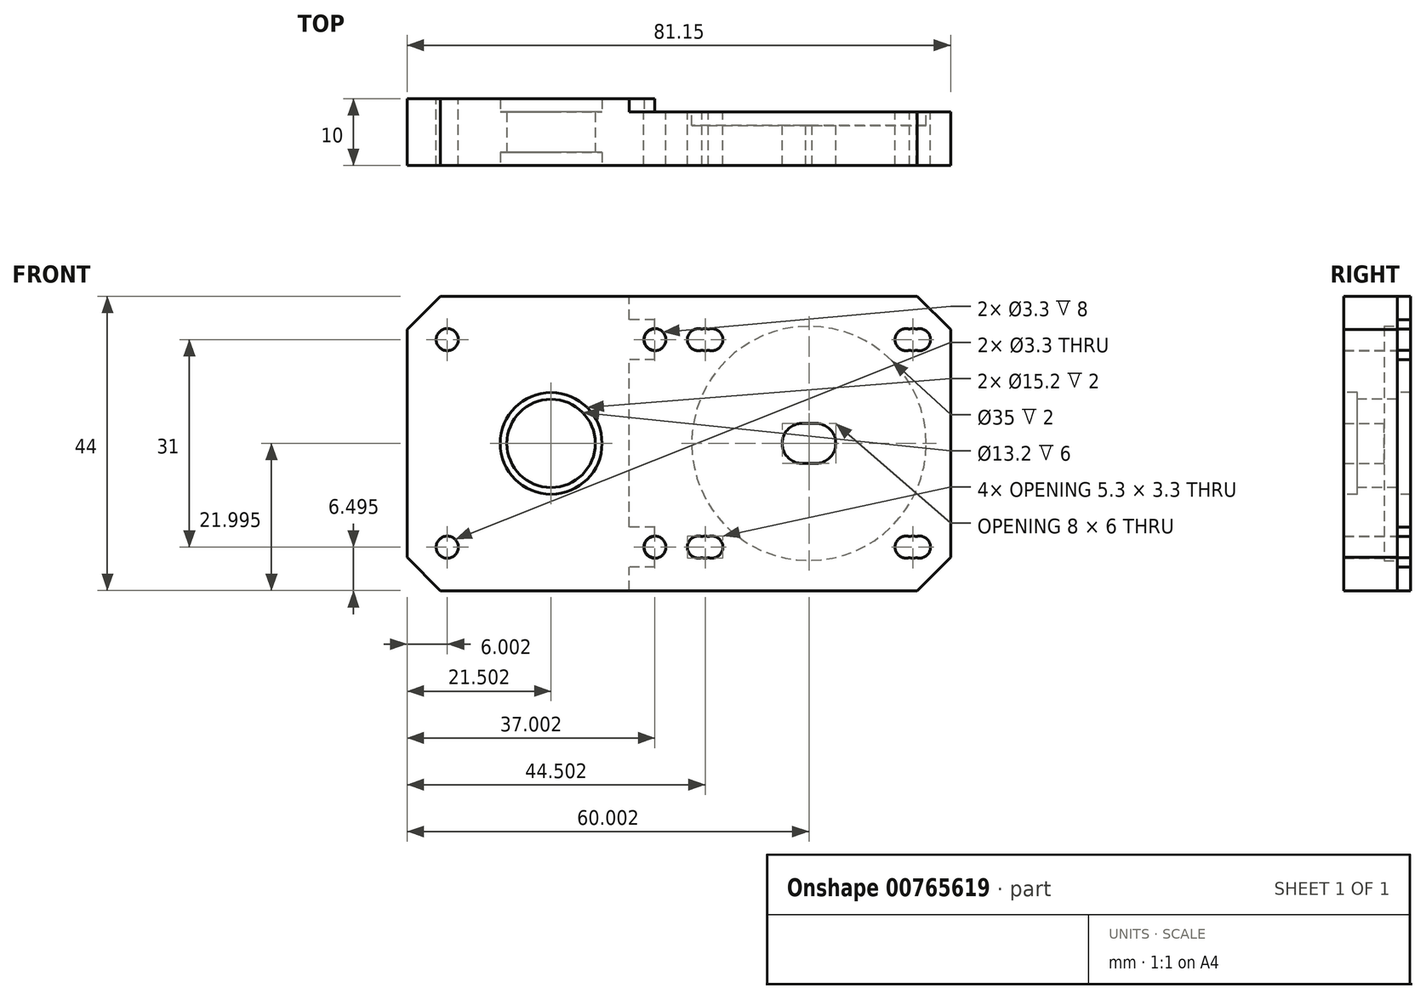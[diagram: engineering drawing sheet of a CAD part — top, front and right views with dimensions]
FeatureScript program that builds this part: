
annotation { "Feature Type Name" : "Feature", "Feature Type Description" : "" }
export const myFeature = defineFeature(function(context is Context, id is Id, definition is map)
    precondition{}
    {
        {
            var Q0;
            Q0=qCreatedBy(makeId("Front.planeOp"),FACE);
            var sketch = newSketch(context, id + "F0", { "sketchPlane" : qUnion([Q0])});
            skLineSegment(sketch, "E0.bottom", {"start": v(-213.07, -45.16) * mm, "end": v(-131.92, -45.16) * mm});
            skLineSegment(sketch, "E0.top", {"start": v(-213.07, -89.16) * mm, "end": v(-131.92, -89.16) * mm});
            skLineSegment(sketch, "E0.left", {"start": v(-213.07, -45.16) * mm, "end": v(-213.07, -89.16) * mm});
            skLineSegment(sketch, "E0.right", {"start": v(-131.92, -45.16) * mm, "end": v(-131.92, -89.16) * mm});
            skLineSegment(sketch, "E1", {"start": v(-131.92, -67.16) * mm, "end": v(-153.07, -67.16) * mm, "construction": true});
            skArc(sketch, "E2", {"start": v(-153.57, -70.12) * mm, "mid": v(-153.07, -70.16) * mm, "end": v(-152.57, -70.12) * mm});
            skLineSegment(sketch, "E3", {"start": v(-153.07, -67.16) * mm, "end": v(-191.57, -67.16) * mm, "construction": true});
            skCircle(sketch, "E4", {"center": v(-191.57, -67.16) * mm, "radius": 3 * mm});
            skLineSegment(sketch, "E5", {"start": v(-191.57, -67.16) * mm, "end": v(-213.07, -67.16) * mm, "construction": true});
            skLineSegment(sketch, "E6.bottom", {"start": v(-137.57, -82.66) * mm, "end": v(-168.57, -82.66) * mm, "construction": true});
            skLineSegment(sketch, "E6.top", {"start": v(-137.57, -51.66) * mm, "end": v(-168.57, -51.66) * mm, "construction": true});
            skLineSegment(sketch, "E6.left", {"start": v(-137.57, -82.66) * mm, "end": v(-137.57, -51.66) * mm, "construction": true});
            skLineSegment(sketch, "E6.right", {"start": v(-168.57, -82.66) * mm, "end": v(-168.57, -51.66) * mm, "construction": true});
            skArc(sketch, "E7", {"start": v(-169.07, -53.24) * mm, "mid": v(-168.57, -53.31) * mm, "end": v(-168.07, -53.24) * mm});
            skArc(sketch, "E8", {"start": v(-138.07, -53.24) * mm, "mid": v(-137.57, -53.31) * mm, "end": v(-137.07, -53.24) * mm});
            skArc(sketch, "E9", {"start": v(-169.07, -84.24) * mm, "mid": v(-168.57, -84.31) * mm, "end": v(-168.07, -84.24) * mm});
            skArc(sketch, "E10", {"start": v(-138.07, -84.24) * mm, "mid": v(-137.57, -84.31) * mm, "end": v(-137.07, -84.24) * mm});
            skLineSegment(sketch, "E11.bottom", {"start": v(-176.07, -51.66) * mm, "end": v(-207.07, -51.66) * mm, "construction": true});
            skLineSegment(sketch, "E11.top", {"start": v(-176.07, -82.66) * mm, "end": v(-207.07, -82.66) * mm, "construction": true});
            skLineSegment(sketch, "E11.left", {"start": v(-176.07, -51.66) * mm, "end": v(-176.07, -82.66) * mm, "construction": true});
            skLineSegment(sketch, "E11.right", {"start": v(-207.07, -51.66) * mm, "end": v(-207.07, -82.66) * mm, "construction": true});
            skCircle(sketch, "E12", {"center": v(-176.07, -51.66) * mm, "radius": 1.65 * mm});
            skCircle(sketch, "E13", {"center": v(-207.07, -51.66) * mm, "radius": 1.65 * mm});
            skCircle(sketch, "E14", {"center": v(-207.07, -82.66) * mm, "radius": 1.65 * mm});
            skCircle(sketch, "E15", {"center": v(-176.07, -82.66) * mm, "radius": 1.65 * mm});
            skLineSegment(sketch, "E16", {"start": v(-168.57, -51.66) * mm, "end": v(-169.57, -51.66) * mm, "construction": true});
            skLineSegment(sketch, "E17", {"start": v(-169.57, -51.66) * mm, "end": v(-168.57, -51.66) * mm, "construction": true});
            skLineSegment(sketch, "E18", {"start": v(-167.57, -51.66) * mm, "end": v(-168.57, -51.66) * mm, "construction": true});
            skArc(sketch, "E19", {"start": v(-168.07, -53.24) * mm, "mid": v(-165.92, -51.66) * mm, "end": v(-168.07, -50.1) * mm});
            skArc(sketch, "E20", {"start": v(-169.07, -50.1) * mm, "mid": v(-171.22, -51.66) * mm, "end": v(-169.07, -53.24) * mm});
            skArc(sketch, "E21.MirrorC", {"start": v(-168.07, -81.1) * mm, "mid": v(-165.92, -82.66) * mm, "end": v(-168.07, -84.24) * mm});
            skArc(sketch, "E22.MirrorC", {"start": v(-169.07, -84.24) * mm, "mid": v(-171.22, -82.66) * mm, "end": v(-169.07, -81.1) * mm});
            skLineSegment(sketch, "E23", {"start": v(-153.07, -51.66) * mm, "end": v(-153.07, -82.66) * mm, "construction": true});
            skArc(sketch, "E24.MirrorC", {"start": v(-138.07, -53.24) * mm, "mid": v(-140.22, -51.66) * mm, "end": v(-138.07, -50.1) * mm});
            skArc(sketch, "E25.MirrorC", {"start": v(-137.07, -50.1) * mm, "mid": v(-134.92, -51.66) * mm, "end": v(-137.07, -53.24) * mm});
            skArc(sketch, "E26.MirrorC", {"start": v(-137.07, -84.24) * mm, "mid": v(-134.92, -82.66) * mm, "end": v(-137.07, -81.1) * mm});
            skArc(sketch, "E27.MirrorC", {"start": v(-138.07, -81.1) * mm, "mid": v(-140.22, -82.66) * mm, "end": v(-138.07, -84.24) * mm});
            skArc(sketch, "E28.trimOffspring", {"start": v(-168.07, -50.1) * mm, "mid": v(-168.57, -50.01) * mm, "end": v(-169.07, -50.1) * mm});
            skArc(sketch, "E29.trimOffspring", {"start": v(-168.07, -81.1) * mm, "mid": v(-168.57, -81.01) * mm, "end": v(-169.07, -81.1) * mm});
            skArc(sketch, "E30.trimOffspring", {"start": v(-137.07, -81.1) * mm, "mid": v(-137.57, -81.01) * mm, "end": v(-138.07, -81.1) * mm});
            skArc(sketch, "E31.trimOffspring", {"start": v(-137.07, -50.1) * mm, "mid": v(-137.57, -50.01) * mm, "end": v(-138.07, -50.1) * mm});
            skLineSegment(sketch, "E32", {"start": v(-153.07, -67.16) * mm, "end": v(-154.07, -67.16) * mm, "construction": true});
            skLineSegment(sketch, "E33", {"start": v(-153.07, -67.16) * mm, "end": v(-152.07, -67.16) * mm, "construction": true});
            skArc(sketch, "E34", {"start": v(-152.57, -70.12) * mm, "mid": v(-149.07, -67.16) * mm, "end": v(-152.57, -64.2) * mm});
            skArc(sketch, "E35", {"start": v(-153.57, -64.2) * mm, "mid": v(-157.07, -67.16) * mm, "end": v(-153.57, -70.12) * mm});
            skArc(sketch, "E36.trimOffspring", {"start": v(-152.57, -64.2) * mm, "mid": v(-153.07, -64.16) * mm, "end": v(-153.57, -64.2) * mm});
            skSolve(sketch);
        }
        {
            var Q0;
            Q0 = qSketchRegion(id + "F0", true);
            extrude(context, id + "F1", {"entities" : qUnion([Q0]), "depth" : 8 * mm, "offsetDistance" : 25 * mm});
        }
        {
            var Q0;
            Q0=makeQuery(id+"F1.opExtrude","CAP_FACE",FACE,{"disambiguationData":[OSD([sQuery(id+"F0.wireOp",EDGE,"E0.bottom"),sQuery(id+"F0.wireOp",EDGE,"E0.top"),sQuery(id+"F0.wireOp",EDGE,"E0.left"),sQuery(id+"F0.wireOp",EDGE,"E0.right"),sQuery(id+"F0.wireOp",EDGE,"E2"),sQuery(id+"F0.wireOp",EDGE,"E4"),sQuery(id+"F0.wireOp",EDGE,"E7"),sQuery(id+"F0.wireOp",EDGE,"E8"),sQuery(id+"F0.wireOp",EDGE,"E9"),sQuery(id+"F0.wireOp",EDGE,"E10")])],"isStart":true});
            var sketch = newSketch(context, id + "F2", { "sketchPlane" : qUnion([Q0])});
            skCircle(sketch, "E37", {"center": v(153.07, -67.16) * mm, "radius": 17.5 * mm});
            skSolve(sketch);
        }
        {
            var Q0;
            Q0 = qSketchRegion(id + "F2", true);
            extrude(context, id + "F3", {"entities" : qUnion([Q0]), "operationType" : NewBodyOperationType.REMOVE, "oppositeDirection" : true, "depth" : 2 * mm, "offsetDistance" : 25 * mm});
        }
        {
            var Q0;
            Q0=makeQuery(id+"F1.opExtrude","CAP_FACE",FACE,{"disambiguationData":[OSD([sQuery(id+"F0.wireOp",EDGE,"E0.bottom"),sQuery(id+"F0.wireOp",EDGE,"E0.top"),sQuery(id+"F0.wireOp",EDGE,"E0.left"),sQuery(id+"F0.wireOp",EDGE,"E0.right"),sQuery(id+"F0.wireOp",EDGE,"E2"),sQuery(id+"F0.wireOp",EDGE,"E4"),sQuery(id+"F0.wireOp",EDGE,"E7"),sQuery(id+"F0.wireOp",EDGE,"E8"),sQuery(id+"F0.wireOp",EDGE,"E9"),sQuery(id+"F0.wireOp",EDGE,"E10")])],"isStart":true});
            var sketch = newSketch(context, id + "F4", { "sketchPlane" : qUnion([Q0])});
            skLineSegment(sketch, "E38.bottom", {"start": v(131.92, -89.16) * mm, "end": v(179.92, -89.16) * mm, "construction": true});
            skLineSegment(sketch, "E38.top", {"start": v(131.92, -45.16) * mm, "end": v(179.92, -45.16) * mm, "construction": true});
            skLineSegment(sketch, "E38.left", {"start": v(131.92, -89.16) * mm, "end": v(131.92, -45.16) * mm, "construction": true});
            skLineSegment(sketch, "E38.right", {"start": v(179.92, -89.16) * mm, "end": v(179.92, -45.16) * mm, "construction": true});
            skLineSegment(sketch, "E39.bottom", {"start": v(213.07, -89.16) * mm, "end": v(179.92, -89.16) * mm});
            skLineSegment(sketch, "E39.top", {"start": v(213.07, -45.16) * mm, "end": v(179.92, -45.16) * mm});
            skLineSegment(sketch, "E39.left", {"start": v(213.07, -89.16) * mm, "end": v(213.07, -45.16) * mm});
            skLineSegment(sketch, "E39.right", {"start": v(179.92, -89.16) * mm, "end": v(179.92, -45.16) * mm});
            skCircle(sketch, "E40", {"center": v(191.57, -67.16) * mm, "radius": 7.6 * mm});
            skCircle(sketch, "E41", {"center": v(207.07, -82.66) * mm, "radius": 1.65 * mm});
            skCircle(sketch, "E42", {"center": v(207.07, -51.66) * mm, "radius": 1.65 * mm});
            skSolve(sketch);
        }
        {
            var Q0;
            Q0 = qSketchRegion(id + "F4", true);
            extrude(context, id + "F5", {"entities" : qUnion([Q0]), "operationType" : NewBodyOperationType.ADD, "depth" : 2 * mm, "offsetDistance" : 25 * mm});
        }
        {
            var Q0;
            Q0=makeQuery(id+"F5.opExtrude","CAP_FACE",FACE,{"disambiguationData":[OSD([sQuery(id+"F4.wireOp",EDGE,"E39.bottom"),sQuery(id+"F4.wireOp",EDGE,"E39.top"),sQuery(id+"F4.wireOp",EDGE,"E39.left"),sQuery(id+"F4.wireOp",EDGE,"E39.right"),sQuery(id+"F4.wireOp",EDGE,"E40")])],"isStart":false});
            var sketch = newSketch(context, id + "F6", { "sketchPlane" : qUnion([Q0])});
            skCircle(sketch, "E43", {"center": v(191.57, -67.16) * mm, "radius": 6.5 * mm});
            skSolve(sketch);
        }
        {
            var Q0;
            Q0 = qSketchRegion(id + "F6", true);
            extrude(context, id + "F7", {"entities" : qUnion([Q0]), "operationType" : NewBodyOperationType.REMOVE, "oppositeDirection" : true, "depth" : 3 * mm, "offsetDistance" : 25 * mm});
        }
        {
            var Q0;
            Q0=makeQuery(id+"F1.opExtrude","CAP_FACE",FACE,{"disambiguationData":[OSD([sQuery(id+"F0.wireOp",EDGE,"E0.bottom"),sQuery(id+"F0.wireOp",EDGE,"E0.top"),sQuery(id+"F0.wireOp",EDGE,"E0.left"),sQuery(id+"F0.wireOp",EDGE,"E0.right"),sQuery(id+"F0.wireOp",EDGE,"E2"),sQuery(id+"F0.wireOp",EDGE,"E4"),sQuery(id+"F0.wireOp",EDGE,"E7"),sQuery(id+"F0.wireOp",EDGE,"E8"),sQuery(id+"F0.wireOp",EDGE,"E9"),sQuery(id+"F0.wireOp",EDGE,"E10")])],"isStart":false});
            var sketch = newSketch(context, id + "F8", { "sketchPlane" : qUnion([Q0])});
            skCircle(sketch, "E44", {"center": v(-191.57, -67.16) * mm, "radius": 7.6 * mm});
            skSolve(sketch);
        }
        {
            var Q0;
            Q0 = qSketchRegion(id + "F8", true);
            extrude(context, id + "F9", {"entities" : qUnion([Q0]), "operationType" : NewBodyOperationType.REMOVE, "oppositeDirection" : true, "depth" : 2 * mm, "offsetDistance" : 25 * mm});
        }
        {
            var Q0;
            Q0=makeQuery(id+"F1.opExtrude","CAP_FACE",FACE,{"disambiguationData":[OSD([sQuery(id+"F0.wireOp",EDGE,"E0.bottom"),sQuery(id+"F0.wireOp",EDGE,"E0.top"),sQuery(id+"F0.wireOp",EDGE,"E0.left"),sQuery(id+"F0.wireOp",EDGE,"E0.right"),sQuery(id+"F0.wireOp",EDGE,"E2"),sQuery(id+"F0.wireOp",EDGE,"E4"),sQuery(id+"F0.wireOp",EDGE,"E7"),sQuery(id+"F0.wireOp",EDGE,"E8"),sQuery(id+"F0.wireOp",EDGE,"E9"),sQuery(id+"F0.wireOp",EDGE,"E10"),sQuery(id+"F0.wireOp",EDGE,"E12"),sQuery(id+"F0.wireOp",EDGE,"E13"),sQuery(id+"F0.wireOp",EDGE,"E14"),sQuery(id+"F0.wireOp",EDGE,"E15"),sQuery(id+"F0.wireOp",EDGE,"E19"),sQuery(id+"F0.wireOp",EDGE,"E20"),sQuery(id+"F0.wireOp",EDGE,"E21.MirrorC"),sQuery(id+"F0.wireOp",EDGE,"E22.MirrorC"),sQuery(id+"F0.wireOp",EDGE,"E24.MirrorC"),sQuery(id+"F0.wireOp",EDGE,"E25.MirrorC"),sQuery(id+"F0.wireOp",EDGE,"E26.MirrorC"),sQuery(id+"F0.wireOp",EDGE,"E27.MirrorC"),sQuery(id+"F0.wireOp",EDGE,"E28.trimOffspring"),sQuery(id+"F0.wireOp",EDGE,"E29.trimOffspring"),sQuery(id+"F0.wireOp",EDGE,"E30.trimOffspring"),sQuery(id+"F0.wireOp",EDGE,"E31.trimOffspring"),sQuery(id+"F0.wireOp",EDGE,"E34"),sQuery(id+"F0.wireOp",EDGE,"E35"),sQuery(id+"F0.wireOp",EDGE,"E36.trimOffspring")])],"isStart":false});
            var sketch = newSketch(context, id + "F10", { "sketchPlane" : qUnion([Q0])});
            skCircle(sketch, "E45", {"center": v(-191.57, -67.16) * mm, "radius": 6.6 * mm});
            skSolve(sketch);
        }
        {
            var Q0;
            Q0 = qSketchRegion(id + "F10", true);
            extrude(context, id + "F11", {"entities" : qUnion([Q0]), "operationType" : NewBodyOperationType.REMOVE, "oppositeDirection" : true, "depth" : 10 * mm, "offsetDistance" : 25 * mm});
        }
        {
            var Q0;
            {var subQ0=sQuery(id+"F0.wireOp",EDGE,"E31.trimOffspring");var subQ1=sQuery(id+"F0.wireOp",EDGE,"E29.trimOffspring");var subQ2=sQuery(id+"F0.wireOp",EDGE,"E28.trimOffspring");var subQ3=sQuery(id+"F0.wireOp",EDGE,"E26.MirrorC");var subQ4=sQuery(id+"F0.wireOp",EDGE,"E25.MirrorC");var subQ5=sQuery(id+"F0.wireOp",EDGE,"E24.MirrorC");var subQ6=sQuery(id+"F0.wireOp",EDGE,"E22.MirrorC");var subQ7=sQuery(id+"F0.wireOp",EDGE,"E21.MirrorC");var subQ8=sQuery(id+"F0.wireOp",EDGE,"E20");var subQ9=sQuery(id+"F0.wireOp",EDGE,"E7");var subQ10=sQuery(id+"F0.wireOp",EDGE,"E30.trimOffspring");var subQ11=sQuery(id+"F0.wireOp",EDGE,"E0.top");var subQ12=sQuery(id+"F0.wireOp",EDGE,"E0.right");var subQ13=sQuery(id+"F0.wireOp",EDGE,"E19");var subQ14=sQuery(id+"F0.wireOp",EDGE,"E27.MirrorC");var subQ15=sQuery(id+"F0.wireOp",EDGE,"E0.bottom");var subQ16=sQuery(id+"F0.wireOp",EDGE,"E10");var subQ17=sQuery(id+"F0.wireOp",EDGE,"E8");var subQ18=sQuery(id+"F0.wireOp",EDGE,"E9");var subQ19=sQuery(id+"F0.wireOp",EDGE,"E12");var subQ20=sQuery(id+"F0.wireOp",EDGE,"E15");Q0=makeQuery(id+"F5.boolean.opBoolean","SPLIT",FACE,{"disambiguationData":[TD([makeQuery(id+"F1.opExtrude","SWEPT_FACE",FACE,{"disambiguationData":[OSD([subQ15])]})])],"derivedFrom":makeQuery(id+"F1.opExtrude","CAP_FACE",FACE,{"disambiguationData":[OSD([subQ15,subQ11,sQuery(id+"F0.wireOp",EDGE,"E0.left"),subQ12,sQuery(id+"F0.wireOp",EDGE,"E2"),sQuery(id+"F0.wireOp",EDGE,"E4"),subQ9,subQ17,subQ18,subQ16,subQ19,sQuery(id+"F0.wireOp",EDGE,"E13"),sQuery(id+"F0.wireOp",EDGE,"E14"),subQ20,subQ13,subQ8,subQ7,subQ6,subQ5,subQ4,subQ3,subQ14,subQ2,subQ1,subQ10,subQ0,sQuery(id+"F0.wireOp",EDGE,"E34"),sQuery(id+"F0.wireOp",EDGE,"E35"),sQuery(id+"F0.wireOp",EDGE,"E36.trimOffspring")])],"isStart":true})});}
            var sketch = newSketch(context, id + "F12", { "sketchPlane" : qUnion([Q0])});
            skArc(sketch, "E46", {"start": v(176.07, -84.26) * mm, "mid": v(177.67, -82.66) * mm, "end": v(176.07, -81.06) * mm});
            skLineSegment(sketch, "E47", {"start": v(176.07, -79.66) * mm, "end": v(179.92, -79.66) * mm});
            skLineSegment(sketch, "E48", {"start": v(176.07, -85.66) * mm, "end": v(179.92, -85.66) * mm});
            skLineSegment(sketch, "E49", {"start": v(179.92, -85.66) * mm, "end": v(179.92, -79.66) * mm});
            skLineSegment(sketch, "E50", {"start": v(179.92, -67.16) * mm, "end": v(131.92, -67.16) * mm, "construction": true});
            skLineSegment(sketch, "E51.MirrorCS", {"start": v(176.07, -54.66) * mm, "end": v(179.92, -54.66) * mm});
            skLineSegment(sketch, "E52.MirrorCS", {"start": v(176.07, -48.66) * mm, "end": v(179.92, -48.66) * mm});
            skArc(sketch, "E53.MirrorC", {"start": v(176.07, -50.06) * mm, "mid": v(177.67, -51.66) * mm, "end": v(176.07, -53.26) * mm});
            skLineSegment(sketch, "E54", {"start": v(179.92, -54.66) * mm, "end": v(179.92, -48.66) * mm});
            skLineSegment(sketch, "E55", {"start": v(176.07, -54.66) * mm, "end": v(176.07, -53.26) * mm});
            skLineSegment(sketch, "E56", {"start": v(176.07, -85.66) * mm, "end": v(176.07, -84.26) * mm});
            skPoint(sketch, "E57.MirrorCS.end.orphan", {"position": v(176.07, -48.66) * mm});
            skPoint(sketch, "E57.MirrorCS.start.orphan", {"position": v(176.07, -54.66) * mm});
            skLineSegment(sketch, "E58.trimOffspring", {"start": v(176.07, -50.06) * mm, "end": v(176.07, -48.66) * mm});
            skLineSegment(sketch, "E59.trimOffspring", {"start": v(176.07, -81.06) * mm, "end": v(176.07, -79.66) * mm});
            skSolve(sketch);
        }
        {
            var Q0;
            Q0 = qSketchRegion(id + "F12", true);
            extrude(context, id + "F13", {"entities" : qUnion([Q0]), "operationType" : NewBodyOperationType.ADD, "depth" : 2 * mm, "offsetDistance" : 25 * mm});
        }
        {
            var Q0;
            Q0=makeQuery(id+"F5.boolean.opBoolean","MERGE",EDGE,{"derivedFrom":[makeQuery(id+"F1.opExtrude","SWEPT_EDGE",EDGE,{"disambiguationData":[OSD([sQuery(id+"F0.wireOp",EDGE,"E0.top"),sQuery(id+"F0.wireOp",EDGE,"E0.left")])]}),makeQuery(id+"F5.opExtrude","SWEPT_EDGE",EDGE,{"disambiguationData":[OSD([sQuery(id+"F4.wireOp",EDGE,"E39.bottom"),sQuery(id+"F4.wireOp",EDGE,"E39.left")])]})]});
            var Q1;
            Q1=makeQuery(id+"F5.boolean.opBoolean","MERGE",EDGE,{"derivedFrom":[makeQuery(id+"F1.opExtrude","SWEPT_EDGE",EDGE,{"disambiguationData":[OSD([sQuery(id+"F0.wireOp",EDGE,"E0.bottom"),sQuery(id+"F0.wireOp",EDGE,"E0.left")])]}),makeQuery(id+"F5.opExtrude","SWEPT_EDGE",EDGE,{"disambiguationData":[OSD([sQuery(id+"F4.wireOp",EDGE,"E39.top"),sQuery(id+"F4.wireOp",EDGE,"E39.left")])]})]});
            var Q2;
            Q2=makeQuery(id+"F1.opExtrude","SWEPT_EDGE",EDGE,{"disambiguationData":[OSD([sQuery(id+"F0.wireOp",EDGE,"E0.top"),sQuery(id+"F0.wireOp",EDGE,"E0.right")])]});
            var Q3;
            Q3=makeQuery(id+"F1.opExtrude","SWEPT_EDGE",EDGE,{"disambiguationData":[OSD([sQuery(id+"F0.wireOp",EDGE,"E0.bottom"),sQuery(id+"F0.wireOp",EDGE,"E0.right")])]});
            chamfer(context, id + "F14", {"entities" : qUnion([Q0, Q1, Q2, Q3]), "width" : 5 * mm, "tangentPropagation" : true});
        }
    });
